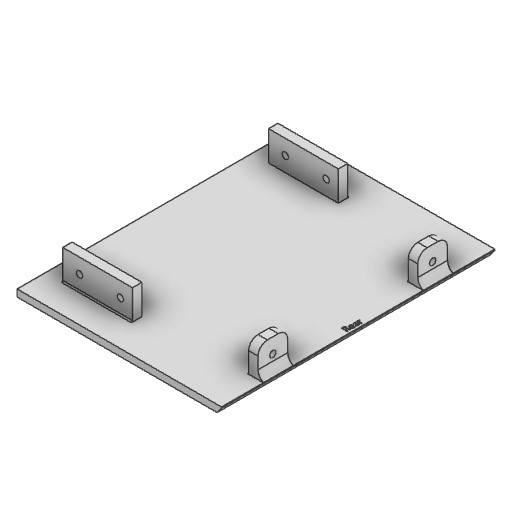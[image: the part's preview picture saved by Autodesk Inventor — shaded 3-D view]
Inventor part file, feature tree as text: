
AUTODESK INVENTOR PART (.ipt)
format: ipt  version: 2025 (Build 290162000, 162)  size: 370,688 bytes
history: native  units: mm
features: sketch x10, extrude x9, projected_geometry x8, other x5, reference x3, fillet x2, mirror x1
ambient origin geometry x8: Origin, YZ Plane, XZ Plane, XY Plane, X Axis, Y Axis, Z Axis, Center Point
bodies: Solid1 (feature_tree)
feature tree (38):
  extrude  "Extrusion1"  Depth=234.0mm
  extrude  "Extrusion2"  Depth=6.0mm
  extrude  "Extrusion3"  Depth=25.4mm TaperAngle=0.0deg
  fillet  "Fillet1"  Radius=1.0mm
  extrude  "Extrusion4"  Depth=25.4mm TaperAngle=0.0deg
  extrude  "Extrusion5"  Depth=8.0mm
  mirror  "Mirror1"
  extrude  "Extrusion8"  Depth=25.4mm
  extrude  "Extrusion9"  Depth=10.0mm
  fillet  "Fillet2"  Radius=155.0mm
  extrude  "Extrusion6"  Depth=76.2mm
  extrude  "Extrusion7"  Depth=8.0mm TaperAngle=0.0deg
  sketch  "Sketch1"  dims[d0=175.0mm d1=234.0mm]
  sketch  "Sketch2"  dims[d5=8.0mm d6=25.4mm d7=0.0mm d8=1.0mm]
  projected_geometry  "Projected Loop1"
  sketch  "Sketch3"  dims[d9=5.5mm d10=25.4mm d11=0.0mm]
  projected_geometry  "Projected Loop2"
  sketch  "Sketch4"  dims[d12=8.0mm d14=8.0mm]
  projected_geometry  "Projected Loop3"
  reference  "Reference3"
  reference  "Reference4"
  sketch  "Sketch5"  dims[d15=25.4mm d16=0.0mm d17=5.5mm]
  projected_geometry  "Projected Loop4"
  sketch  "Sketch Rectangular Pattern1"  dims[d2=6.0mm d3=0.0mm d4=26.4mm]
  sketch  "Sketch6"  dims[d18=25.4mm d19=0.0mm d20=30.0mm d22=35.0mm d23=10.0mm d25=10.0mm d27=155.0mm]
  projected_geometry  "Projected Loop5"
  sketch  "Sketch7"  dims[d28=55.0mm d29=76.2mm]
  projected_geometry  "Projected Loop6"
  sketch  "Sketch8"  dims[d30=5.0mm d31=8.0mm d32=0.0mm]
  reference  "Reference5"
  projected_geometry  "Projected Loop7"
  sketch  "Sketch9"  dims[d33=2.0mm d34=0.0mm d35=0.0mm d36=0.0mm d37=0.4mm d38=0.0mm d39=1.0mm]
  projected_geometry  "Projected Loop8"
  other  "<userpath>\Desktop\puppycat\woodhouseMK1.iam"
  other  "woodhouseMK1.iam"
  other  "10inStrut:2"
  other  "4844N105_T-Slotted Framing Structural Bracket:1"
  other  "lowerRearBracket:1"
